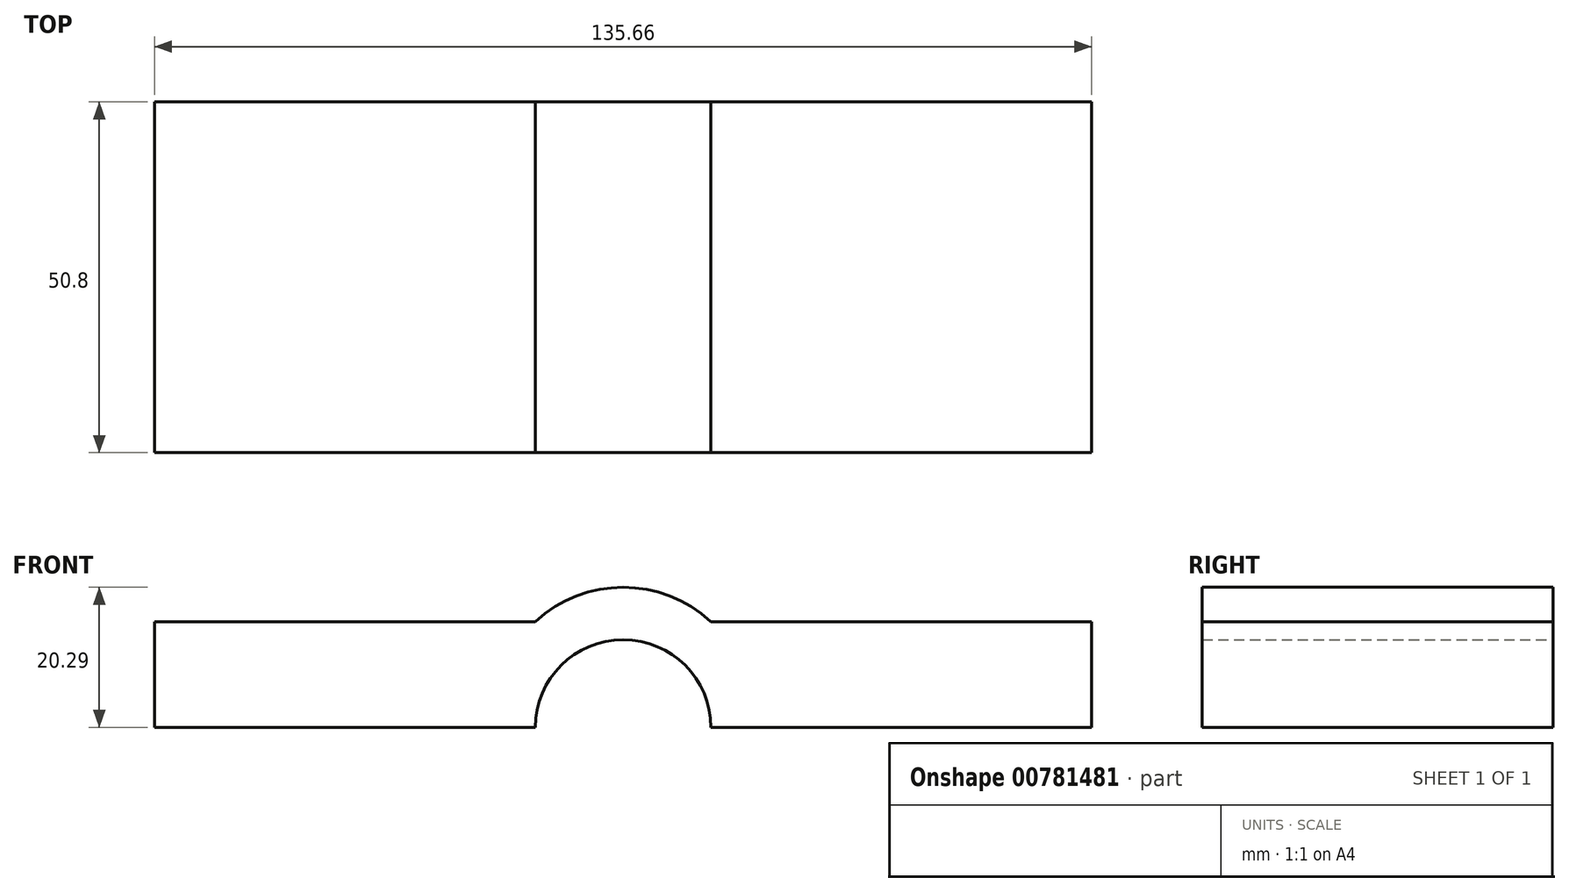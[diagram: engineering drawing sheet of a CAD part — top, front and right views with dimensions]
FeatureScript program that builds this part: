
annotation { "Feature Type Name" : "Feature", "Feature Type Description" : "" }
export const myFeature = defineFeature(function(context is Context, id is Id, definition is map)
    precondition{}
    {
        {
            var Q0;
            Q0=qCreatedBy(makeId("Front.planeOp"),FACE);
            var sketch = newSketch(context, id + "F0", { "sketchPlane" : qUnion([Q0])});
            skLineSegment(sketch, "E0.bottom", {"start": v(-67.83, 0) * mm, "end": v(-12.7, 0) * mm});
            skLineSegment(sketch, "E0.top", {"start": v(-67.83, 15.31) * mm, "end": v(-12.7, 15.31) * mm});
            skLineSegment(sketch, "E0.left", {"start": v(-67.83, 0) * mm, "end": v(-67.83, 15.31) * mm});
            skLineSegment(sketch, "E0.right", {"start": v(-12.7, 0) * mm, "end": v(-12.7, 15.31) * mm});
            skLineSegment(sketch, "E1.MirrorCS", {"start": v(67.83, 0) * mm, "end": v(12.7, 0) * mm});
            skLineSegment(sketch, "E2.MirrorCS", {"start": v(12.7, 0) * mm, "end": v(12.7, 15.31) * mm});
            skLineSegment(sketch, "E3.MirrorCS", {"start": v(67.83, 15.31) * mm, "end": v(12.7, 15.31) * mm});
            skLineSegment(sketch, "E4.MirrorCS", {"start": v(67.83, 0) * mm, "end": v(67.83, 15.31) * mm});
            skArc(sketch, "E5", {"start": v(12.7, 15.31) * mm, "mid": v(0, 20.29) * mm, "end": v(-12.7, 15.31) * mm});
            skArc(sketch, "E6", {"start": v(12.7, 0) * mm, "mid": v(0, 12.7) * mm, "end": v(-12.7, 0) * mm});
            skSolve(sketch);
        }
        {
            var Q0;
            Q0=makeQuery(id+"F0.imprint","IMPRINT",FACE,{"disambiguationData":[TD([[makeQuery(id+"F0.imprint","IMPRINT",EDGE,{"derivedFrom":sQuery(id+"F0.wireOp",EDGE,"E0.bottom")}),1.0]])]});
            var Q1;
            Q1=makeQuery(id+"F0.imprint","IMPRINT",FACE,{"disambiguationData":[TD([[makeQuery(id+"F0.imprint","IMPRINT",EDGE,{"derivedFrom":sQuery(id+"F0.wireOp",EDGE,"E0.right")}),-1.0]])]});
            var Q2;
            Q2=makeQuery(id+"F0.imprint","IMPRINT",FACE,{"disambiguationData":[TD([[makeQuery(id+"F0.imprint","IMPRINT",EDGE,{"derivedFrom":sQuery(id+"F0.wireOp",EDGE,"E1.MirrorCS")}),-1.0]])]});
            extrude(context, id + "F1", {"entities" : qUnion([Q0, Q1, Q2]), "depth" : 50.8 * mm, "offsetDistance" : 25.4 * mm});
        }
    });
